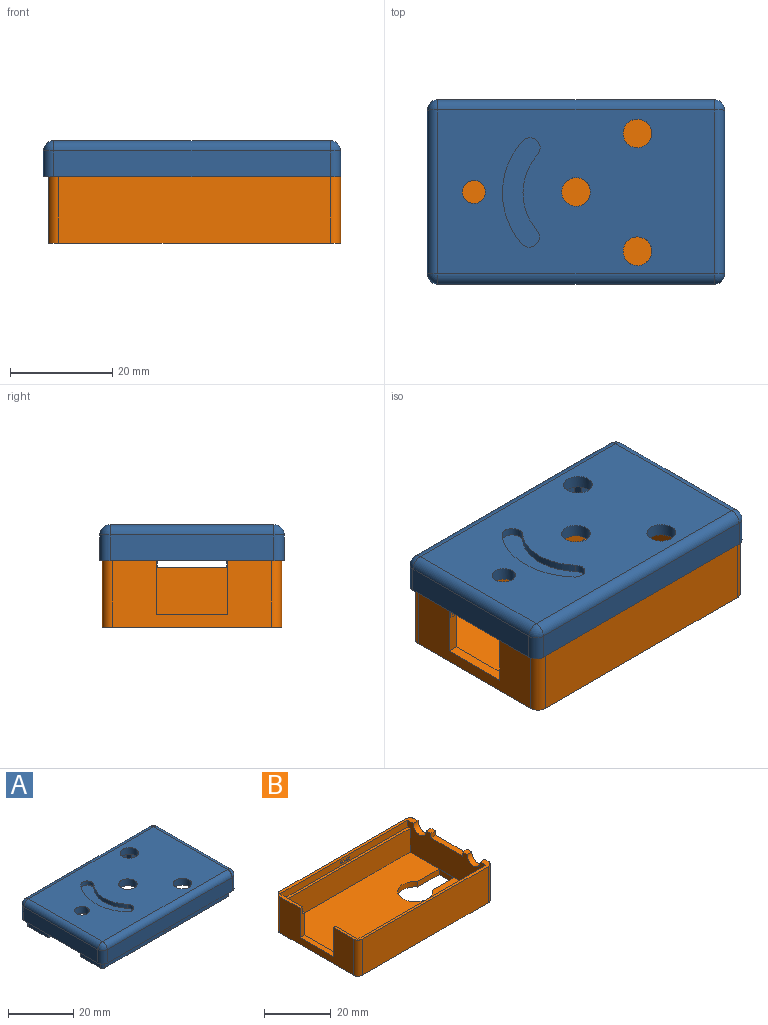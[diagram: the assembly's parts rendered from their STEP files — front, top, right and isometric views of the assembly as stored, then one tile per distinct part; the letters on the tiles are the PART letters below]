
ASSEMBLY  parts=2 mates=1
PART A: 108 faces, bbox 58x36x9.8 mm
  f0: plane 8.52x2.8mm, normal (-1,0,0), area 23.8mm2, adj f1,f6,f105,f106
  f1: plane 54.52x9.52mm, normal (0,0,-1), area 62.8mm2, adj f0,f2,f3,f4,f80,f105,f106
  f2: plane 8.52x2.8mm, normal (1,0,0), area 23.8mm2, adj f1,f4,f6,f106
  f3: plane 55.45x2.8mm, normal (0,-1,0), area 147.6mm2, adj f1,f6,f79,f80,f92,f99,f100,f101
  f4: plane 55.52x2.8mm, normal (0,1,0), area 149.8mm2, adj f1,f2,f6,f79,f80
  f5: plane 53.52x9.52mm, normal (0,0,-1), area 61.8mm2, adj f75,f76,f77,f78,f93,f104,f107
  f6: plane 58x36mm, normal (0,0,-1), area 244.4mm2, adj f0,f2,f3,f4,f7,f9,f10,f11
  f7: plane 8.1x4.53mm, normal (0,1,0), area 36.7mm2, adj f6,f8,f18,f73
  f8: plane 55.5x31mm, normal (0,0,-1), area 1531mm2, adj f7,f9,f10,f14,f15,f16,f17,f18
  f9: plane 37.41x4.53mm, normal (0,1,0), area 169.4mm2, adj f6,f8,f31,f71
  f10: plane 8.75x4.53mm, normal (-1,0,0), area 27.2mm2, adj f6,f8,f15,f20,f22,f28
  f11: plane 32x5.03mm, normal (-1,0,0), area 160.9mm2, adj f6,f81,f83,f84
  f12: plane 54x5.03mm, normal (0,1,0), area 271.5mm2, adj f6,f81,f85,f86
  f13: plane 54x5.03mm, normal (0,-1,0), area 271.5mm2, adj f6,f83,f89,f92
  f14: plane 32x5.05mm, normal (1,0,0), area 74.7mm2, adj f6,f8,f19,f20,f21,f22,f28,f29
  f15: plane 53x4.53mm, normal (0,-1,0), area 240mm2, adj f6,f8,f10,f16
  f16: plane 31x4.53mm, normal (1,0,0), area 140.4mm2, adj f6,f8,f15,f17
  f17: plane 4.53x0.48mm, normal (0,1,0), area 2.2mm2, adj f6,f8,f16,f32
  f18: plane 8.75x4.53mm, normal (-1,0,0), area 27mm2, adj f6,f7,f8,f19,f21,f29
  f19: cylinder r=2.75mm len=5.5mm, axis (1,0,0), area 22.3mm2, adj f6,f14,f18,f29
  f20: cylinder r=2.75mm len=5.5mm, axis (1,0,0), area 22.1mm2, adj f6,f10,f14,f28
  f21: plane 4.53x2.5mm, normal (0,1,0), area 11.3mm2, adj f8,f14,f18,f29
  f22: plane 4.53x2.5mm, normal (0,-1,0), area 11.3mm2, adj f8,f10,f14,f28
  f23: plane 54x32mm, normal (0,0,1), area 1549.7mm2, adj f24,f25,f26,f27,f55,f56,f57,f58
  f24: cylinder r=2.8mm len=5.6mm, axis (0,0,1), area 44mm2, adj f8,f23
  f25: cylinder r=2.8mm len=5.6mm, axis (0,0,1), area 44mm2, adj f8,f23
  f26: cylinder r=2.8mm len=5.6mm, axis (0,0,1), area 44mm2, adj f8,f23
  f27: cylinder r=2.25mm len=4.5mm, axis (0,0,1), area 35.3mm2, adj f8,f23
  f28: plane 2.5x1.87mm, normal (0,0,-1), area 4.7mm2, adj f10,f14,f20,f22
  f29: plane 2.5x1.88mm, normal (0,0,-1), area 4.7mm2, adj f14,f18,f19,f21
  f30: plane 3.5x2.27mm, normal (0,-1,0), area 8mm2, adj f6,f31,f32,f34
  f31: plane 6.8x2mm, normal (1,0,0), area 13.6mm2, adj f8,f9,f30,f33,f34
  f32: plane 6.8x2mm, normal (-1,0,0), area 13.6mm2, adj f8,f17,f30,f33,f34
  f33: plane 6.8x3.5mm, normal (0,1,0), area 23.8mm2, adj f8,f31,f32,f34
  f34: plane 3.5x2mm, normal (0,0,-1), area 7mm2, adj f30,f31,f32,f33
  f35: plane 6.8x2mm, normal (1,0,0), area 13.6mm2, adj f8,f36,f38,f39
  f36: plane 6.8x3.5mm, normal (0,-1,0), area 23.8mm2, adj f8,f35,f37,f39
  f37: plane 6.8x2mm, normal (-1,0,0), area 13.6mm2, adj f8,f36,f38,f39
  f38: plane 6.8x3.5mm, normal (0,1,0), area 23.8mm2, adj f8,f35,f37,f39
  f39: plane 3.5x2mm, normal (0,0,-1), area 7mm2, adj f35,f36,f37,f38
  f40: plane 6.8x2mm, normal (1,0,0), area 13.6mm2, adj f8,f41,f43,f44
  f41: plane 6.8x3.5mm, normal (0,-1,0), area 23.8mm2, adj f8,f40,f42,f44
  f42: plane 6.8x2mm, normal (-1,0,0), area 13.6mm2, adj f8,f41,f43,f44
  f43: plane 6.8x3.5mm, normal (0,1,0), area 23.8mm2, adj f8,f40,f42,f44
  f44: plane 3.5x2mm, normal (0,0,-1), area 7mm2, adj f40,f41,f42,f43
  f45: plane 6.8x2mm, normal (-1,0,0), area 13.6mm2, adj f8,f46,f48,f49
  f46: plane 6.8x3.5mm, normal (0,1,0), area 23.8mm2, adj f8,f45,f47,f49
  f47: plane 6.8x2mm, normal (1,0,0), area 13.6mm2, adj f8,f46,f48,f49
  f48: plane 6.8x3.5mm, normal (0,-1,0), area 23.8mm2, adj f8,f45,f47,f49
  f49: plane 3.5x2mm, normal (0,0,-1), area 7mm2, adj f45,f46,f47,f48
  f50: plane 6.8x3.5mm, normal (0,1,0), area 23.8mm2, adj f8,f51,f53,f54
  f51: plane 6.8x2mm, normal (1,0,0), area 13.6mm2, adj f8,f50,f52,f54
  f52: plane 6.8x3.5mm, normal (0,-1,0), area 23.8mm2, adj f8,f51,f53,f54
  f53: plane 6.8x2mm, normal (-1,0,0), area 13.6mm2, adj f8,f50,f52,f54
  f54: plane 3.5x2mm, normal (0,0,-1), area 7mm2, adj f50,f51,f52,f53
  f55: cylinder r=11.14mm len=14.73mm, axis (0,0,1), area 24.1mm2, adj f23,f56,f58,f59
  f56: cylinder r=2mm len=3.49mm, axis (0,0,1), area 9.4mm2, adj f23,f55,f57,f59
  f57: cylinder r=15.14mm len=20.02mm, axis (0,0,1), area 32.8mm2, adj f23,f56,f58,f59
  f58: cylinder r=2mm len=3.51mm, axis (0,0,1), area 9.4mm2, adj f23,f55,f57,f59
  f59: plane 21.37x7.34mm, normal (0,0,1), area 88.5mm2, adj f55,f56,f57,f58
  f60: plane 6.8x2mm, normal (-1,0,0), area 13.6mm2, adj f8,f61,f63,f64
  f61: plane 6.8x3.5mm, normal (0,1,0), area 23.8mm2, adj f8,f60,f62,f64
  f62: plane 6.8x2mm, normal (1,0,0), area 13.6mm2, adj f8,f61,f63,f64
  f63: plane 6.8x3.5mm, normal (0,-1,0), area 23.8mm2, adj f8,f60,f62,f64
  f64: plane 3.5x2mm, normal (0,0,-1), area 7mm2, adj f60,f61,f62,f63
  f65: plane 6.8x2mm, normal (-1,0,0), area 13.6mm2, adj f8,f66,f68,f69
  f66: plane 6.8x3.5mm, normal (0,1,0), area 23.8mm2, adj f8,f65,f67,f69
  f67: plane 6.8x2mm, normal (1,0,0), area 13.6mm2, adj f8,f66,f68,f69
  f68: plane 6.8x3.5mm, normal (0,-1,0), area 23.8mm2, adj f8,f65,f67,f69
  f69: plane 3.5x2mm, normal (0,0,-1), area 7mm2, adj f65,f66,f67,f68
  f70: plane 3.5x2.27mm, normal (0,-1,0), area 8mm2, adj f6,f71,f73,f74
  f71: plane 6.8x2mm, normal (-1,0,0), area 13.6mm2, adj f8,f9,f70,f72,f74
  f72: plane 6.8x3.5mm, normal (0,1,0), area 23.8mm2, adj f8,f71,f73,f74
  f73: plane 6.8x2mm, normal (1,0,0), area 13.6mm2, adj f7,f8,f70,f72,f74
  f74: plane 3.5x2mm, normal (0,0,-1), area 7mm2, adj f70,f71,f72,f73
  f75: plane 52.52x2.8mm, normal (0,1,0), area 144.7mm2, adj f5,f6,f93,f94,f95,f96,f97,f104
  f76: plane 52.52x2.8mm, normal (0,-1,0), area 147mm2, adj f5,f6,f77,f93
  f77: plane 8.52x2.8mm, normal (1,0,0), area 23.8mm2, adj f5,f6,f76,f107
  f78: plane 8.52x2.8mm, normal (-1,0,0), area 23.8mm2, adj f5,f6,f104,f107
  f79: plane 2x1mm, normal (0,0,-1), area 2mm2, adj f3,f4,f14,f80,f92
  f80: plane 2.77x1mm, normal (1,0,0), area 2.8mm2, adj f1,f3,f4,f79
  f81: cylinder r=2mm len=5.03mm, axis (0,0,-1), area 15.8mm2, adj f6,f11,f12,f82
  f82: sphere r=2mm, area 6.3mm2, adj f81,f84,f85
  f83: cylinder r=2mm len=5.03mm, axis (0,0,1), area 15.8mm2, adj f6,f11,f13,f87
  f84: cylinder r=2mm len=32mm, axis (0,1,0), area 100.5mm2, adj f11,f23,f82,f87
  f85: cylinder r=2mm len=54mm, axis (1,0,0), area 169.6mm2, adj f12,f23,f82,f88
  f86: cylinder r=2mm len=5.03mm, axis (0,0,1), area 15.8mm2, adj f6,f12,f14,f88
  f87: sphere r=2mm, area 8.6mm2, adj f83,f84,f89
  f88: sphere r=2mm, area 6.3mm2, adj f85,f86,f90
  f89: cylinder r=2mm len=54mm, axis (-1,0,0), area 169.6mm2, adj f13,f23,f87,f91
  f90: cylinder r=2mm len=32mm, axis (0,-1,0), area 100.5mm2, adj f14,f23,f88,f91
  f91: sphere r=2mm, area 4mm2, adj f89,f90,f92
  f92: cylinder r=2mm len=5.05mm, axis (0,0,-1), area 15.8mm2, adj f3,f6,f13,f14,f79,f91
  f93: plane 2.8x1mm, normal (1,0,0), area 2.8mm2, adj f5,f6,f75,f76
  f94: plane 0.75x0.3mm, normal (1,0,0), area 0.2mm2, adj f75,f95,f97,f98
  f95: plane 3x0.3mm, normal (0,0,-1), area 0.9mm2, adj f75,f94,f96,f98
  f96: plane 0.75x0.3mm, normal (-1,0,0), area 0.2mm2, adj f75,f95,f97,f98
  f97: plane 3x0.3mm, normal (0,0,1), area 0.9mm2, adj f75,f94,f96,f98
  f98: plane 3x0.75mm, normal (0,1,0), area 2.2mm2, adj f94,f95,f96,f97
  f99: plane 0.75x0.3mm, normal (-1,0,0), area 0.2mm2, adj f3,f100,f102,f103
  f100: plane 3x0.3mm, normal (0,0,-1), area 0.9mm2, adj f3,f99,f101,f103
  f101: plane 0.75x0.3mm, normal (1,0,0), area 0.2mm2, adj f3,f100,f102,f103
  f102: plane 3x0.3mm, normal (0,0,1), area 0.9mm2, adj f3,f99,f101,f103
  f103: plane 3x0.75mm, normal (0,-1,0), area 2.3mm2, adj f99,f100,f101,f102
  f104: cylinder r=1mm len=2.8mm, axis (0,0,-1), area 4.4mm2, adj f5,f6,f75,f78
  f105: cylinder r=1mm len=2.8mm, axis (0,0,-1), area 4.4mm2, adj f0,f1,f3,f6
  f106: plane 2.8x1mm, normal (0,1,0), area 2.8mm2, adj f0,f1,f2,f6
  f107: plane 2.8x1mm, normal (0,-1,0), area 2.8mm2, adj f5,f6,f77,f78
PART B: 46 faces, bbox 57x35x13.2 mm
  f0: plane 54x2.5mm, normal (0,-1,0), area 131.5mm2, adj f5,f8,f28,f29,f41,f42,f43,f44
  f1: plane 54x2.5mm, normal (0,1,0), area 131.5mm2, adj f3,f8,f30,f31,f36,f37,f38,f39
  f2: plane 10.75x2mm, normal (0,1,0), area 19mm2, adj f3,f7,f13,f23,f30,f31
  f3: plane 57x10.5mm, normal (0,0,1), area 69.5mm2, adj f1,f2,f7,f8,f9,f11,f16,f30
  f4: plane 10.75x2mm, normal (0,-1,0), area 19mm2, adj f5,f7,f13,f23,f28,f29
  f5: plane 57x10.5mm, normal (0,0,1), area 69.5mm2, adj f0,f4,f7,f8,f10,f11,f15,f28
  f6: plane 57x35mm, normal (0,0,-1), area 1852.5mm2, adj f7,f9,f10,f11,f24,f25,f26,f27
  f7: plane 31x13.23mm, normal (-1,0,0), area 259.6mm2, adj f2,f3,f4,f5,f6,f23,f33,f34
  f8: plane 33x11.23mm, normal (-1,0,0), area 307.4mm2, adj f0,f1,f3,f5,f12,f14,f15,f16
  f9: plane 53x13.23mm, normal (0,-1,0), area 701.1mm2, adj f3,f6,f32,f33
  f10: plane 53x13.23mm, normal (0,1,0), area 701.1mm2, adj f5,f6,f34,f35
  f11: plane 31x13.23mm, normal (1,0,0), area 364.4mm2, adj f3,f5,f6,f15,f16,f17,f18,f20
  f12: plane 53x8.73mm, normal (0,1,0), area 462.6mm2, adj f8,f13,f19,f31
  f13: plane 31x8.73mm, normal (1,0,0), area 155.1mm2, adj f2,f4,f12,f14,f19,f23,f29,f31
  f14: plane 53x8.73mm, normal (0,-1,0), area 462.6mm2, adj f8,f13,f19,f29
  f15: cylinder r=2.75mm len=5.5mm, axis (1,0,0), area 17.8mm2, adj f5,f8,f11,f22
  f16: cylinder r=2.75mm len=5.5mm, axis (1,0,0), area 17.7mm2, adj f3,f8,f11,f21
  f17: plane 2x1.53mm, normal (0,-1,0), area 3.1mm2, adj f8,f11,f20,f22
  f18: plane 2x1.53mm, normal (0,1,0), area 3.1mm2, adj f8,f11,f20,f21
  f19: plane 53x31mm, normal (0,0,1), area 1503.9mm2, adj f8,f12,f13,f14,f24,f25,f26,f27
  f20: plane 13.5x2mm, normal (0,0,1), area 27mm2, adj f8,f11,f17,f18
  f21: plane 2x1.87mm, normal (0,0,1), area 3.7mm2, adj f8,f11,f16,f18
  f22: plane 2x1.88mm, normal (0,0,1), area 3.8mm2, adj f8,f11,f15,f17
  f23: plane 14x2mm, normal (0,0,1), area 28mm2, adj f2,f4,f7,f13
  f24: cylinder r=5.25mm len=10.5mm, axis (0,0,1), area 52.5mm2, adj f6,f19,f25,f26
  f25: plane 9.05x2mm, normal (0,-1,0), area 18.1mm2, adj f6,f19,f24,f27
  f26: plane 9.05x2mm, normal (0,1,0), area 18.1mm2, adj f6,f19,f24,f27
  f27: plane 6.3x2mm, normal (-1,0,0), area 12.6mm2, adj f6,f19,f25,f26
  f28: plane 9.5x2.5mm, normal (1,0,0), area 23.8mm2, adj f0,f4,f5,f29
  f29: plane 54x9.5mm, normal (0,0,1), area 62.5mm2, adj f0,f4,f8,f13,f14,f28
  f30: plane 9.5x2.5mm, normal (1,0,0), area 23.8mm2, adj f1,f2,f3,f31
  f31: plane 54x9.5mm, normal (0,0,1), area 62.5mm2, adj f1,f2,f8,f12,f13,f30
  f32: cylinder r=2mm len=13.23mm, axis (0,0,-1), area 41.6mm2, adj f3,f6,f9,f11
  f33: cylinder r=2mm len=13.23mm, axis (0,0,1), area 41.6mm2, adj f3,f6,f7,f9
  f34: cylinder r=2mm len=13.23mm, axis (0,0,-1), area 41.6mm2, adj f5,f6,f7,f10
  f35: cylinder r=2mm len=13.23mm, axis (0,0,1), area 41.6mm2, adj f5,f6,f10,f11
  f36: plane 1x0.4mm, normal (1,0,0), area 0.4mm2, adj f1,f37,f39,f40
  f37: plane 3.5x0.4mm, normal (0,0,-1), area 1.4mm2, adj f1,f36,f38,f40
  f38: plane 1x0.4mm, normal (-1,0,0), area 0.4mm2, adj f1,f37,f39,f40
  f39: plane 3.5x0.4mm, normal (0,0,1), area 1.4mm2, adj f1,f36,f38,f40
  f40: plane 3.5x1mm, normal (0,1,0), area 3.5mm2, adj f36,f37,f38,f39
  f41: plane 1x0.4mm, normal (-1,0,0), area 0.4mm2, adj f0,f42,f44,f45
  f42: plane 3.5x0.4mm, normal (0,0,-1), area 1.4mm2, adj f0,f41,f43,f45
  f43: plane 1x0.4mm, normal (1,0,0), area 0.4mm2, adj f0,f42,f44,f45
  f44: plane 3.5x0.4mm, normal (0,0,1), area 1.4mm2, adj f0,f41,f43,f45
  f45: plane 3.5x1mm, normal (0,-1,0), area 3.5mm2, adj f41,f42,f43,f44
PLACE A rot(axis=(-1,0,0),0deg) t=(9.79,14.57,20.33)mm
PLACE B t=(10.29,14.57,20.6)mm fixed
MATE fastened B.f16 <-> A.f19  axis (1,0,0) through (38.79,3.2,15.04)mm
